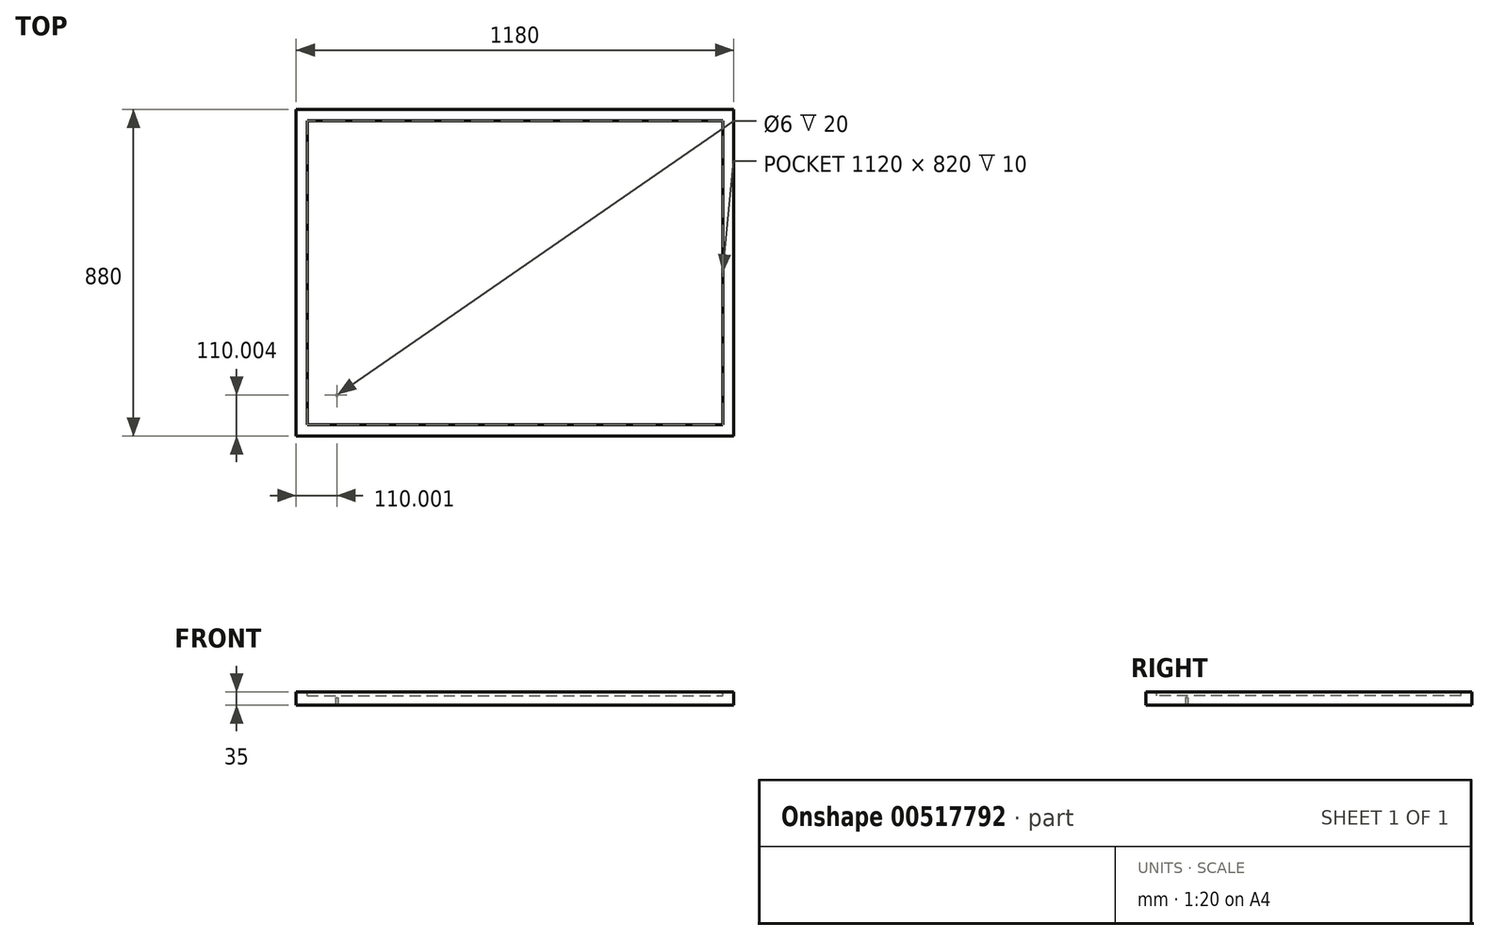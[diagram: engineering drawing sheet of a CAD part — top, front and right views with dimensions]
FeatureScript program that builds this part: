
annotation { "Feature Type Name" : "Feature", "Feature Type Description" : "" }
export const myFeature = defineFeature(function(context is Context, id is Id, definition is map)
    precondition{}
    {
        {
            var Q0;
            Q0=qCreatedBy(makeId("Top.planeOp"),FACE);
            var sketch = newSketch(context, id + "F0", { "sketchPlane" : qUnion([Q0])});
            skLineSegment(sketch, "E0.bottom", {"start": v(-1126.93, 852.95) * mm, "end": v(53.07, 852.95) * mm});
            skLineSegment(sketch, "E0.top", {"start": v(-1126.93, -27.05) * mm, "end": v(53.07, -27.05) * mm});
            skLineSegment(sketch, "E0.left", {"start": v(-1126.93, 852.95) * mm, "end": v(-1126.93, -27.05) * mm});
            skLineSegment(sketch, "E0.right", {"start": v(53.07, 852.95) * mm, "end": v(53.07, -27.05) * mm});
            skSolve(sketch);
        }
        {
            var Q0;
            Q0=makeQuery(id+"F0.imprint","IMPRINT",FACE,{"disambiguationData":[TD([[makeQuery(id+"F0.imprint","IMPRINT",EDGE,{"derivedFrom":sQuery(id+"F0.wireOp",EDGE,"E0.bottom")}),-1.0]])]});
            extrude(context, id + "F1", {"entities" : qUnion([Q0]), "depth" : 35 * mm, "offsetDistance" : 25 * mm});
        }
        {
            var Q0;
            Q0=makeQuery(id+"F1.opExtrude","CAP_FACE",FACE,{"disambiguationData":[OSD([sQuery(id+"F0.wireOp",EDGE,"E0.bottom"),sQuery(id+"F0.wireOp",EDGE,"E0.top"),sQuery(id+"F0.wireOp",EDGE,"E0.left"),sQuery(id+"F0.wireOp",EDGE,"E0.right")])],"isStart":true});
            var sketch = newSketch(context, id + "F2", { "sketchPlane" : qUnion([Q0])});
            skCircle(sketch, "E1", {"center": v(-1016.93, -82.95) * mm, "radius": 3 * mm});
            skSolve(sketch);
        }
        {
            var Q0;
            Q0=makeQuery(id+"F2.imprint","IMPRINT",FACE,{"disambiguationData":[TD([[makeQuery(id+"F2.imprint","IMPRINT",EDGE,{"derivedFrom":sQuery(id+"F2.wireOp",EDGE,"E1")}),1.0]])]});
            extrude(context, id + "F3", {"entities" : qUnion([Q0]), "operationType" : NewBodyOperationType.REMOVE, "oppositeDirection" : true, "depth" : 20 * mm, "offsetDistance" : 25 * mm});
        }
        {
            var Q0;
            Q0=makeQuery(id+"F1.opExtrude","CAP_FACE",FACE,{"disambiguationData":[OSD([sQuery(id+"F0.wireOp",EDGE,"E0.bottom"),sQuery(id+"F0.wireOp",EDGE,"E0.top"),sQuery(id+"F0.wireOp",EDGE,"E0.left"),sQuery(id+"F0.wireOp",EDGE,"E0.right")])],"isStart":false});
            var sketch = newSketch(context, id + "F4", { "sketchPlane" : qUnion([Q0])});
            skSolve(sketch);
        }
        {
            var Q0;
            Q0=makeQuery(id+"F4.imprint","IMPRINT",FACE,{"disambiguationData":[TD([[makeQuery(id+"F4.imprint","IMPRINT",EDGE,{"derivedFrom":makeQuery(id+"F1.opExtrude","CAP_EDGE",EDGE,{"disambiguationData":[OSD([sQuery(id+"F0.wireOp",EDGE,"E0.bottom")])],"isStart":false})}),-1.0]])]});
            var sketch = newSketch(context, id + "F5", { "sketchPlane" : qUnion([Q0])});
            skLineSegment(sketch, "E2.bottom", {"start": v(-1096.93, 822.95) * mm, "end": v(23.07, 822.95) * mm});
            skLineSegment(sketch, "E2.top", {"start": v(-1096.93, 2.95) * mm, "end": v(23.07, 2.95) * mm});
            skLineSegment(sketch, "E2.left", {"start": v(-1096.93, 822.95) * mm, "end": v(-1096.93, 2.95) * mm});
            skLineSegment(sketch, "E2.right", {"start": v(23.07, 822.95) * mm, "end": v(23.07, 2.95) * mm});
            skSolve(sketch);
        }
        {
            var Q0;
            Q0=makeQuery(id+"F5.imprint","IMPRINT",FACE,{"disambiguationData":[TD([[makeQuery(id+"F5.imprint","IMPRINT",EDGE,{"derivedFrom":sQuery(id+"F5.wireOp",EDGE,"E2.bottom")}),-1.0]])]});
            extrude(context, id + "F6", {"entities" : qUnion([Q0]), "operationType" : NewBodyOperationType.REMOVE, "oppositeDirection" : true, "depth" : 10 * mm, "offsetDistance" : 25 * mm});
        }
    });
